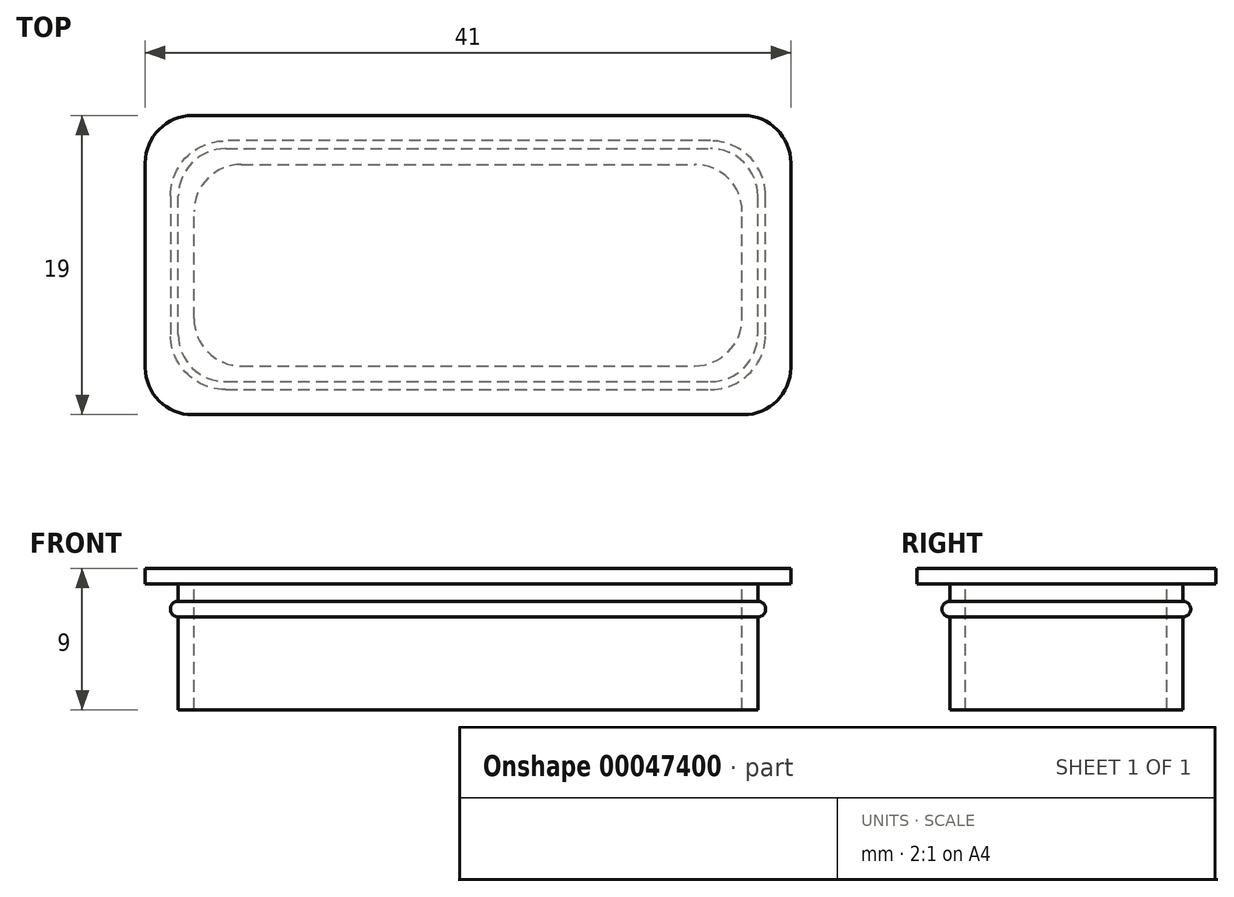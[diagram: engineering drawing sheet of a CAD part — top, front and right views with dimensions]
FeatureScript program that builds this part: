
annotation { "Feature Type Name" : "Feature", "Feature Type Description" : "" }
export const myFeature = defineFeature(function(context is Context, id is Id, definition is map)
    precondition{}
    {
        {
            var Q0;
            Q0=qCreatedBy(makeId("Top.planeOp"),FACE);
            var sketch = newSketch(context, id + "F0", { "sketchPlane" : qUnion([Q0])});
            skLineSegment(sketch, "E0.rect.bottom", {"start": v(20.5, -9.5) * mm, "end": v(-20.5, -9.5) * mm});
            skLineSegment(sketch, "E0.rect.top", {"start": v(20.5, 9.5) * mm, "end": v(-20.5, 9.5) * mm});
            skLineSegment(sketch, "E0.rect.left", {"start": v(20.5, -9.5) * mm, "end": v(20.5, 9.5) * mm});
            skLineSegment(sketch, "E0.rect.right", {"start": v(-20.5, -9.5) * mm, "end": v(-20.5, 9.5) * mm});
            skPoint(sketch, "E0.rect.middle", {"position": v(0, 0) * mm});
            skSolve(sketch);
        }
        {
            var Q0;
            Q0=makeQuery(id+"F0.imprint","IMPRINT",FACE,{"disambiguationData":[TD([[makeQuery(id+"F0.imprint","IMPRINT",EDGE,{"derivedFrom":sQuery(id+"F0.wireOp",EDGE,"E0.rect.bottom")}),-1.0]])]});
            extrude(context, id + "F1", {"entities" : qUnion([Q0]), "endBound" : BoundingType.SYMMETRIC, "depth" : 1 * mm});
        }
        {
            var Q0;
            Q0=makeQuery(id+"F1.opExtrude","CAP_FACE",FACE,{"disambiguationData":[OSD([sQuery(id+"F0.wireOp",EDGE,"E0.rect.bottom"),sQuery(id+"F0.wireOp",EDGE,"E0.rect.top"),sQuery(id+"F0.wireOp",EDGE,"E0.rect.left"),sQuery(id+"F0.wireOp",EDGE,"E0.rect.right")])],"isStart":true});
            var sketch = newSketch(context, id + "F2", { "sketchPlane" : qUnion([Q0])});
            skLineSegment(sketch, "E1.rect.bottom", {"start": v(-18.4, 7.4) * mm, "end": v(18.4, 7.4) * mm});
            skLineSegment(sketch, "E1.rect.top", {"start": v(-18.4, -7.4) * mm, "end": v(18.4, -7.4) * mm});
            skLineSegment(sketch, "E1.rect.left", {"start": v(-18.4, 7.4) * mm, "end": v(-18.4, -7.4) * mm});
            skLineSegment(sketch, "E1.rect.right", {"start": v(18.4, 7.4) * mm, "end": v(18.4, -7.4) * mm});
            skPoint(sketch, "E1.rect.middle", {"position": v(0, 0) * mm});
            skSolve(sketch);
        }
        {
            var Q0;
            Q0=makeQuery(id+"F2.imprint","IMPRINT",FACE,{"disambiguationData":[TD([[makeQuery(id+"F2.imprint","IMPRINT",EDGE,{"derivedFrom":sQuery(id+"F2.wireOp",EDGE,"E1.rect.bottom")}),-1.0]])]});
            extrude(context, id + "F3", {"entities" : qUnion([Q0]), "operationType" : NewBodyOperationType.ADD, "depth" : 8 * mm});
        }
        {
            var Q0;
            Q0=makeQuery(id+"F3.opExtrude","CAP_FACE",FACE,{"disambiguationData":[OSD([sQuery(id+"F2.wireOp",EDGE,"E1.rect.bottom"),sQuery(id+"F2.wireOp",EDGE,"E1.rect.top"),sQuery(id+"F2.wireOp",EDGE,"E1.rect.left"),sQuery(id+"F2.wireOp",EDGE,"E1.rect.right")])],"isStart":false});
            shell(context, id + "F4", {"entities" : qUnion([Q0]), "thickness" : 1 * mm});
        }
        {
            var Q0;
            Q0=makeQuery(id+"F1.opExtrude","SWEPT_EDGE",EDGE,{"disambiguationData":[OSD([sQuery(id+"F0.wireOp",EDGE,"E0.rect.bottom"),sQuery(id+"F0.wireOp",EDGE,"E0.rect.right")])]});
            var Q1;
            Q1=makeQuery(id+"F1.opExtrude","SWEPT_EDGE",EDGE,{"disambiguationData":[OSD([sQuery(id+"F0.wireOp",EDGE,"E0.rect.top"),sQuery(id+"F0.wireOp",EDGE,"E0.rect.right")])]});
            var Q2;
            Q2=makeQuery(id+"F1.opExtrude","SWEPT_EDGE",EDGE,{"disambiguationData":[OSD([sQuery(id+"F0.wireOp",EDGE,"E0.rect.top"),sQuery(id+"F0.wireOp",EDGE,"E0.rect.left")])]});
            var Q3;
            Q3=makeQuery(id+"F1.opExtrude","SWEPT_EDGE",EDGE,{"disambiguationData":[OSD([sQuery(id+"F0.wireOp",EDGE,"E0.rect.bottom"),sQuery(id+"F0.wireOp",EDGE,"E0.rect.left")])]});
            var Q4;
            Q4=makeQuery(id+"F3.opExtrude","SWEPT_EDGE",EDGE,{"disambiguationData":[OSD([sQuery(id+"F2.wireOp",EDGE,"E1.rect.top"),sQuery(id+"F2.wireOp",EDGE,"E1.rect.right")])]});
            var Q5;
            Q5=makeQuery(id+"F3.opExtrude","SWEPT_EDGE",EDGE,{"disambiguationData":[OSD([sQuery(id+"F2.wireOp",EDGE,"E1.rect.top"),sQuery(id+"F2.wireOp",EDGE,"E1.rect.left")])]});
            var Q6;
            Q6=makeQuery(id+"F3.opExtrude","SWEPT_EDGE",EDGE,{"disambiguationData":[OSD([sQuery(id+"F2.wireOp",EDGE,"E1.rect.bottom"),sQuery(id+"F2.wireOp",EDGE,"E1.rect.left")])]});
            var Q7;
            Q7=makeQuery(id+"F3.opExtrude","SWEPT_EDGE",EDGE,{"disambiguationData":[OSD([sQuery(id+"F2.wireOp",EDGE,"E1.rect.bottom"),sQuery(id+"F2.wireOp",EDGE,"E1.rect.right")])]});
            var Q8;
            Q8=makeQuery(id+"F4.opShell","OFFSET_EDGE",EDGE,{"disambiguationData":[OSD([sQuery(id+"F2.wireOp",EDGE,"E1.rect.bottom"),sQuery(id+"F2.wireOp",EDGE,"E1.rect.left")])]});
            var Q9;
            Q9=makeQuery(id+"F4.opShell","OFFSET_EDGE",EDGE,{"disambiguationData":[OSD([sQuery(id+"F2.wireOp",EDGE,"E1.rect.top"),sQuery(id+"F2.wireOp",EDGE,"E1.rect.left")])]});
            var Q10;
            Q10=makeQuery(id+"F4.opShell","OFFSET_EDGE",EDGE,{"disambiguationData":[OSD([sQuery(id+"F2.wireOp",EDGE,"E1.rect.top"),sQuery(id+"F2.wireOp",EDGE,"E1.rect.right")])]});
            var Q11;
            Q11=makeQuery(id+"F4.opShell","OFFSET_EDGE",EDGE,{"disambiguationData":[OSD([sQuery(id+"F2.wireOp",EDGE,"E1.rect.bottom"),sQuery(id+"F2.wireOp",EDGE,"E1.rect.right")])]});
            fillet(context, id + "F5", {"entities" : qUnion([Q0, Q1, Q2, Q3, Q4, Q5, Q6, Q7, Q8, Q9, Q10, Q11]), "radius" : 3 * mm, "tangentPropagation" : true, "allowEdgeOverflow" : false});
        }
        {
            var Q0;
            Q0=makeQuery(id+"F1.opExtrude","CAP_FACE",FACE,{"disambiguationData":[OSD([sQuery(id+"F0.wireOp",EDGE,"E0.rect.bottom"),sQuery(id+"F0.wireOp",EDGE,"E0.rect.top"),sQuery(id+"F0.wireOp",EDGE,"E0.rect.left"),sQuery(id+"F0.wireOp",EDGE,"E0.rect.right")])],"isStart":true});
            cPlane(context, id + "F6", {"entities" : qUnion([Q0]), "cplaneType" : CPlaneType.OFFSET, "offset" : 1.1 * mm, "width" : 150 * mm, "height" : 150 * mm});
        }
        {
            var Q0;
            Q0=qCreatedBy(id+"F6.planeOp",FACE);
            var sketch = newSketch(context, id + "F7", { "sketchPlane" : qUnion([Q0])});
            skLineSegment(sketch, "E2.rect.bottom", {"start": v(-15.4, 7.4) * mm, "end": v(15.4, 7.4) * mm});
            skLineSegment(sketch, "E2.rect.top", {"start": v(-15.4, -7.4) * mm, "end": v(15.4, -7.4) * mm});
            skLineSegment(sketch, "E2.rect.left", {"start": v(-18.4, 4.4) * mm, "end": v(-18.4, -4.4) * mm});
            skLineSegment(sketch, "E2.rect.right", {"start": v(18.4, 4.4) * mm, "end": v(18.4, -4.4) * mm});
            skPoint(sketch, "E2.rect.middle", {"position": v(0, 0) * mm});
            skPoint(sketch, "E3.visualSharp", {"position": v(-18.4, -7.4) * mm});
            skArc(sketch, "E3.filletArc", {"start": v(-18.4, -4.4) * mm, "mid": v(-17.52, -6.52) * mm, "end": v(-15.4, -7.4) * mm});
            skPoint(sketch, "E4.visualSharp", {"position": v(-18.4, 7.4) * mm});
            skArc(sketch, "E4.filletArc", {"start": v(-15.4, 7.4) * mm, "mid": v(-17.52, 6.52) * mm, "end": v(-18.4, 4.4) * mm});
            skPoint(sketch, "E5.visualSharp", {"position": v(18.4, 7.4) * mm});
            skArc(sketch, "E5.filletArc", {"start": v(18.4, 4.4) * mm, "mid": v(17.52, 6.52) * mm, "end": v(15.4, 7.4) * mm});
            skPoint(sketch, "E6.visualSharp", {"position": v(18.4, -7.4) * mm});
            skArc(sketch, "E6.filletArc", {"start": v(15.4, -7.4) * mm, "mid": v(17.52, -6.52) * mm, "end": v(18.4, -4.4) * mm});
            skArc(sketch, "E7.0", {"start": v(-18.9, -4.4) * mm, "mid": v(-17.87, -6.87) * mm, "end": v(-15.4, -7.9) * mm});
            skLineSegment(sketch, "E7.1", {"start": v(-18.9, 4.4) * mm, "end": v(-18.9, -4.4) * mm});
            skLineSegment(sketch, "E7.2", {"start": v(-15.4, -7.9) * mm, "end": v(15.4, -7.9) * mm});
            skArc(sketch, "E7.3", {"start": v(-15.4, 7.9) * mm, "mid": v(-17.87, 6.87) * mm, "end": v(-18.9, 4.4) * mm});
            skArc(sketch, "E7.4", {"start": v(15.4, -7.9) * mm, "mid": v(17.87, -6.87) * mm, "end": v(18.9, -4.4) * mm});
            skLineSegment(sketch, "E7.5", {"start": v(18.9, 4.4) * mm, "end": v(18.9, -4.4) * mm});
            skArc(sketch, "E7.6", {"start": v(18.9, 4.4) * mm, "mid": v(17.87, 6.87) * mm, "end": v(15.4, 7.9) * mm});
            skLineSegment(sketch, "E7.7", {"start": v(-15.4, 7.9) * mm, "end": v(15.4, 7.9) * mm});
            skSolve(sketch);
        }
        {
            var Q0;
            Q0=makeQuery(id+"F7.imprint","IMPRINT",FACE,{"disambiguationData":[TD([[makeQuery(id+"F7.imprint","IMPRINT",EDGE,{"derivedFrom":sQuery(id+"F7.wireOp",EDGE,"E2.rect.bottom")}),1.0]])]});
            extrude(context, id + "F8", {"entities" : qUnion([Q0]), "operationType" : NewBodyOperationType.ADD, "depth" : 1 * mm});
        }
        {
            var Q0;
            Q0=makeQuery(id+"F8.opExtrude","CAP_EDGE",EDGE,{"disambiguationData":[OSD([sQuery(id+"F7.wireOp",EDGE,"E7.2")])],"isStart":false});
            var Q1;
            Q1=makeQuery(id+"F8.opExtrude","CAP_EDGE",EDGE,{"disambiguationData":[OSD([sQuery(id+"F7.wireOp",EDGE,"E7.2")])],"isStart":true});
            fillet(context, id + "F9", {"entities" : qUnion([Q0, Q1]), "radius" : .5 * mm, "tangentPropagation" : true, "allowEdgeOverflow" : false});
        }
    });
